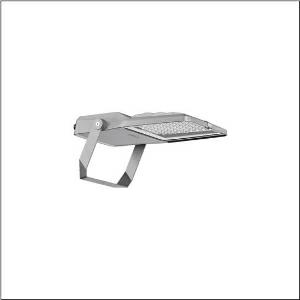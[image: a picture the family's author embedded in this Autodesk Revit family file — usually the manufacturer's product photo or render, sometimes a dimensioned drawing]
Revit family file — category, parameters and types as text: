
# Revit family: floodlight_fl_21_iq_mini___pl61_5xa7772d1c1a_27aa
name_source: partatom
category: Lighting Fixtures
units: mm (PartAtom-declared; Revit-internal decimal feet)

## family parameters
Cut with Voids When Loaded = No
Host = Face
Light Source = No
Part Type = Normal
Room Calculation Point = No
Round Connector Dimension = Use Diameter
Shared = No

## types (1)
- --- (1 x LED, 14490 lm, 143 W, 2200K)
    Apparent Load = 143 VA
    CIE Flux Codes = 33 65 98 100 100
    Color Rendering = 70
    Color Temperature = 2200K
    Default Elevation = 1800 mm
    Description = Floodlight FL 21 iQ mini, floodlight, primary light control with lens, of PMMA, primary optical cover: protective disc, of toughened safety glass, transparent, light distribution: PL61, light emission: direct distribution, installation type: surface-mounted, lamps: LED, High Power LED, rated values: 14.490lm | 143W | 101,3lm/W (begin service life); end service life: 14.490lm | 151,6W; at 50% lumin. flux: 7.245lm | 60,5W | 119,8lm/W, colour temperature: 2200K, colour rendering: CRI > 70, light colour: 722, light setting 1 begin service life: 100% | 14.490lm | 143W | 101,3lm/W | 2.200K, light setting 1 end service life: 151,6W, further light settings possible, control: Street-Remote, Auto-Match, Temp-Guard, Night-Set, Smart-Wire, Desk-Remote (wireless, voltage-free reading and setting of iQ features in the workshop via application-optimized NFC function/RFID function), optimised constant luminous flux control (CLO 2.0), pre-setting: linear dimming characteristic, with terminal, 6-pole, mains connection: 220..240V, AC, 50/60Hz, luminaire housing, of diecast aluminium, powder-coated, SITECO metallic grey (DB 702S), corrosivity category C5 mid according to DIN EN ISO 12944suitable for swimming poolschlorine-resistant, sealing non-destructively replaceable, mounting bracket, of steel, galvanised, powder-coated, SITECO metallic grey (DB 702S), protection rating (complete): IP66, insulation class (complete): insulation class II (safety insulation), certification: CE, ENEC, VDE, protection symbol: D, impact resistance: IK08, permissible operating ambient temperature: -40..+40°C, permissible operating ambient temperature for outdoor applications: -40..+50°C, standard: DIN EN 12944, LABS conformity tested according to VDMA 24364:2018-05, packaging unit: 1 piece

Light Distribution: PL61
    Height = 70 mm
    Lamp = 1 x LED
    Lamp Light Flux = 14490 lm
    Lamp Power = 143 W
    Lamp count = 1
    Length = 485 mm
    Luminous efficacy = 101 lm/W
    Manufacturer = Siteco
    ModVariant = No
    Model = 5XA7772D1C1A
    Number of Poles = 1
    OnlyDefault = Yes
    Power Factor = 1
    Product Name = Floodlight FL 21 iQ mini | PL61
    Product group = floodlight | pylon annexe
    ProductGroupID = 6201
    Protection Class = Protection class II
    Protection Degree = IP 66
    RLX_Detail_Level = 1
    RLX_Emergency_Light_Flux = 0 lm
    RLX_Emergency_Type = 0
    RLX_Emergency_Type_DB = No
    RlxData = <blob elided: 96565 chars, md5=90cde642>
    Socket = socket
    Standby Power = 0 W
    System Light Flux = 14490 lm
    System Power = 143 W
    Type Comments = factory setting: luminous flux: 100 % | dim-lin: 254 | 730 mA
    Type Image = l_1006845.jpg
    URL = http://relux.com
    VarID = @adj_172051
    Voltage = 0 V
    Weight = 0.00 kg
    Width = 337 mm

## geometry (parser evidence)
native form markers: Blend x4, Sweep x14
no freeform markers — native parametric forms only
